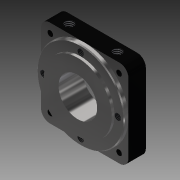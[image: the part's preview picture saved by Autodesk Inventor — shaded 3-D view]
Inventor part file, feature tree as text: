
AUTODESK INVENTOR PART (.ipt)
format: ipt  version: 2013 (Build 170138000, 138)  size: 209,408 bytes
history: native  units: in
note: dims shown in document units (in); Inventor stores cm internally (conversion verified against a paired STEP export)
features: thread x8, extrude x6, sketch x5, fillet x1, chamfer x1
ambient origin geometry x8: Origin, YZ Plane, XZ Plane, XY Plane, X Axis, Y Axis, Z Axis, Center Point
bodies: Solid1 (feature_tree)
feature tree (21):
  sketch  "Sketch1"  dims[d2=1.1024in d7=2.5in]
  extrude  "Extrusion1"  Depth=2.5in
  extrude  "Extrusion2"  Depth=1.063in
  fillet  "Fillet1"  Radius=0.185in
  extrude  "Extrusion3"  Depth=1.063in
  extrude  "Extrusion4"  Depth=2.126in
  thread  "Thread1"  [1 undecoded]
  thread  "Thread2"  [1 undecoded]
  thread  "Thread3"  [1 undecoded]
  thread  "Thread4"  [1 undecoded]
  chamfer  "Chamfer1"  Distance=2.5in
  extrude  "Extrusion5"  Depth=0.1181in TaperAngle=0.0deg
  extrude  "Extrusion6"  Depth=0.0787in TaperAngle=0.0deg
  thread  "Thread5"  [1 undecoded]
  thread  "Thread6"  [1 undecoded]
  thread  "Thread7"  [1 undecoded]
  thread  "Thread8"  [1 undecoded]
  sketch  "Sketch2"  dims[d8=2.5in d9=1.063in d10=0.185in]
  sketch  "Sketch3"  dims[d11=1.063in d12=1.063in]
  sketch  "Sketch4"  dims[d13=1.063in d14=2.126in d15=0.5in d16=0.0in d17=0.1575in d18=0.2756in d19=0.1575in d20=0.0in]
  sketch  "Sketch5"  dims[d21=0.25in d22=2.5in d23=0.1181in d24=0.0in d25=0.0787in d26=0.0in d27=1.0in d28=0.0in d29=1.0in d30=0.0in d31=1.0in d32=0.0in d33=1.0in d34=0.0in d35=0.025in d36=0.125in d37=45.0deg d38=1.378in d40=0.25in d41=0.5in d42=0.0in d43=1.378in d45=0.25in d46=0.5in d47=0.0in d48=1.0in d49=0.0in d50=1.0in d51=0.0in d52=1.0in d53=0.0in d54=1.0in d55=0.0in]
note: 8 required parameter values undecoded (feature->parameter linkage not recoverable at this tier; creation-order binding heuristic only, values carry confidence <= 0.55)
